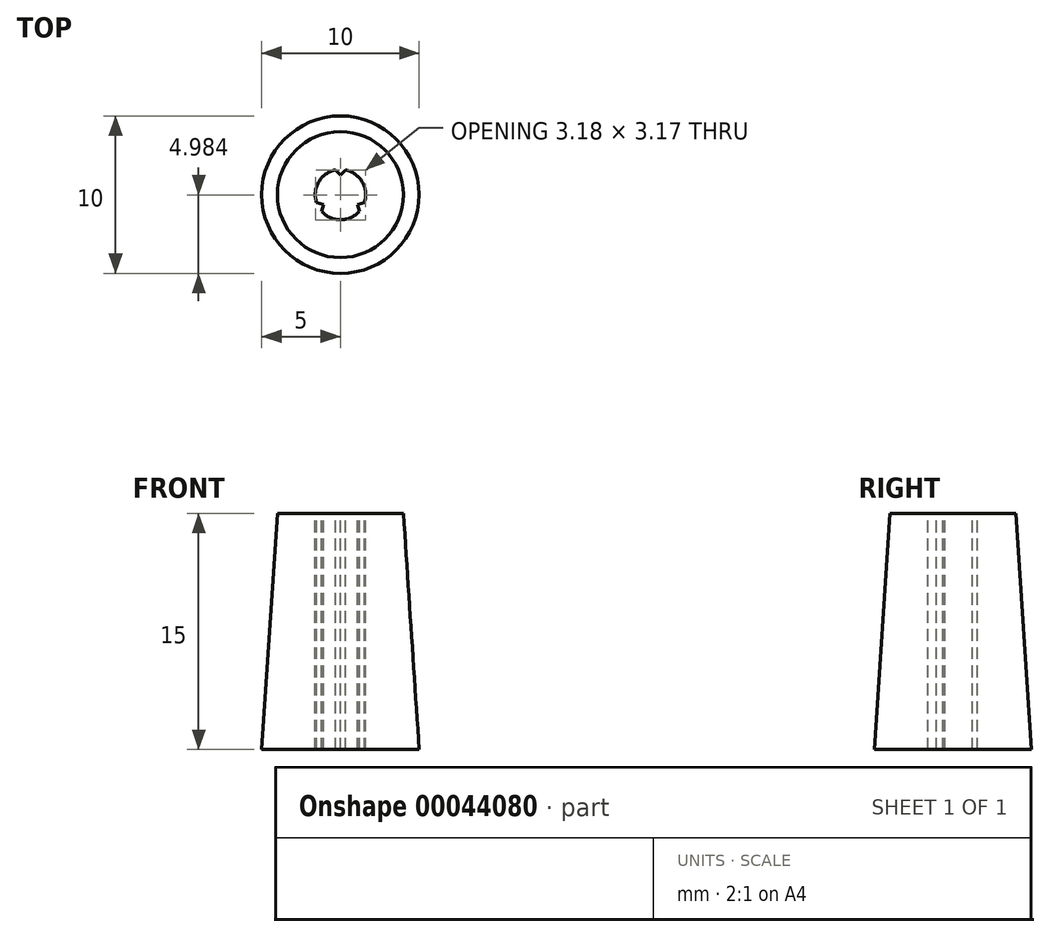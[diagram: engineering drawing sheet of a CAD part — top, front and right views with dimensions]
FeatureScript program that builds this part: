
annotation { "Feature Type Name" : "Feature", "Feature Type Description" : "" }
export const myFeature = defineFeature(function(context is Context, id is Id, definition is map)
    precondition{}
    {
        {
            var Q0;
            Q0=qCreatedBy(makeId("Front.planeOp"),FACE);
            var sketch = newSketch(context, id + "F0", { "sketchPlane" : qUnion([Q0])});
            skLineSegment(sketch, "E0", {"start": v(0, 0) * mm, "end": v(5, 0) * mm});
            skLineSegment(sketch, "E1", {"start": v(5, 0) * mm, "end": v(4, 15) * mm});
            skLineSegment(sketch, "E2", {"start": v(4, 15) * mm, "end": v(0, 15) * mm});
            skLineSegment(sketch, "E3", {"start": v(0, 15) * mm, "end": v(0, 0) * mm});
            skSolve(sketch);
        }
        {
            var Q0;
            Q0=makeQuery(id+"F0.imprint","IMPRINT",FACE,{"disambiguationData":[TD([[makeQuery(id+"F0.imprint","IMPRINT",EDGE,{"derivedFrom":sQuery(id+"F0.wireOp",EDGE,"E0")}),1.0]])]});
            var Q1;
            Q1=sQuery(id+"F0.wireOp",EDGE,"E3");
            revolve(context, id + "F1", {"entities" : qUnion([Q0]), "axis" : qUnion([Q1]), "revolveType" : RevolveType.FULL});
        }
        {
            var Q0;
            Q0=makeQuery(id+"F1.opRevolve","SWEPT_FACE",FACE,{"disambiguationData":[OSD([sQuery(id+"F0.wireOp",EDGE,"E2")])]});
            var sketch = newSketch(context, id + "F2", { "sketchPlane" : qUnion([Q0])});
            skCircle(sketch, "E4", {"center": v(0, 0) * mm, "radius": 1.6 * mm});
            skSolve(sketch);
        }
        {
            var Q0;
            Q0 = qSketchRegion(id + "F2", true);
            extrude(context, id + "F3", {"entities" : qUnion([Q0]), "operationType" : NewBodyOperationType.REMOVE, "endBound" : BoundingType.UP_TO_NEXT, "oppositeDirection" : true, "depth" : 25 * mm});
        }
        {
            var Q0;
            Q0=makeQuery(id+"F1.opRevolve","SWEPT_FACE",FACE,{"disambiguationData":[OSD([sQuery(id+"F0.wireOp",EDGE,"E2")])]});
            var sketch = newSketch(context, id + "F4", { "sketchPlane" : qUnion([Q0])});
            skLineSegment(sketch, "E5", {"start": v(0, 0) * mm, "end": v(0, 1.6) * mm, "construction": true});
            skLineSegment(sketch, "E6", {"start": v(0, 0) * mm, "end": v(-1.39, -0.8) * mm, "construction": true});
            skLineSegment(sketch, "E7", {"start": v(0, 0) * mm, "end": v(1.39, -0.8) * mm, "construction": true});
            skCircle(sketch, "E8", {"center": v(0, 0) * mm, "radius": 1.6 * mm, "construction": true});
            skCircle(sketch, "E9", {"center": v(0, 0) * mm, "radius": 1.25 * mm, "construction": true});
            skLineSegment(sketch, "E10", {"start": v(-0.32, 1.57) * mm, "end": v(0, 1.25) * mm});
            skLineSegment(sketch, "E11", {"start": v(0, 1.25) * mm, "end": v(0.32, 1.57) * mm});
            skArc(sketch, "E12", {"start": v(0.32, 1.57) * mm, "mid": v(0, 1.6) * mm, "end": v(-0.32, 1.57) * mm});
            skLineSegment(sketch, "E13", {"start": v(1.52, -0.5) * mm, "end": v(1.08, -0.62) * mm});
            skLineSegment(sketch, "E14", {"start": v(1.08, -0.62) * mm, "end": v(1.2, -1.06) * mm});
            skLineSegment(sketch, "E15", {"start": v(-1.52, -0.5) * mm, "end": v(-1.08, -0.62) * mm});
            skLineSegment(sketch, "E16", {"start": v(-1.08, -0.62) * mm, "end": v(-1.2, -1.06) * mm});
            skArc(sketch, "E17", {"start": v(1.2, -1.06) * mm, "mid": v(1.39, -0.8) * mm, "end": v(1.52, -0.5) * mm});
            skArc(sketch, "E18", {"start": v(-1.52, -0.5) * mm, "mid": v(-1.39, -0.8) * mm, "end": v(-1.2, -1.06) * mm});
            skSolve(sketch);
        }
        {
            var Q0;
            Q0 = qSketchRegion(id + "F4", true);
            var Q1;
            Q1=makeQuery(id+"F1.opRevolve","SWEPT_FACE",FACE,{"disambiguationData":[OSD([sQuery(id+"F0.wireOp",EDGE,"E0")])]});
            extrude(context, id + "F5", {"entities" : qUnion([Q0]), "operationType" : NewBodyOperationType.ADD, "endBound" : BoundingType.UP_TO_SURFACE, "oppositeDirection" : true, "endBoundEntityFace" : qUnion([Q1]), "depth" : 25 * mm});
        }
    });
